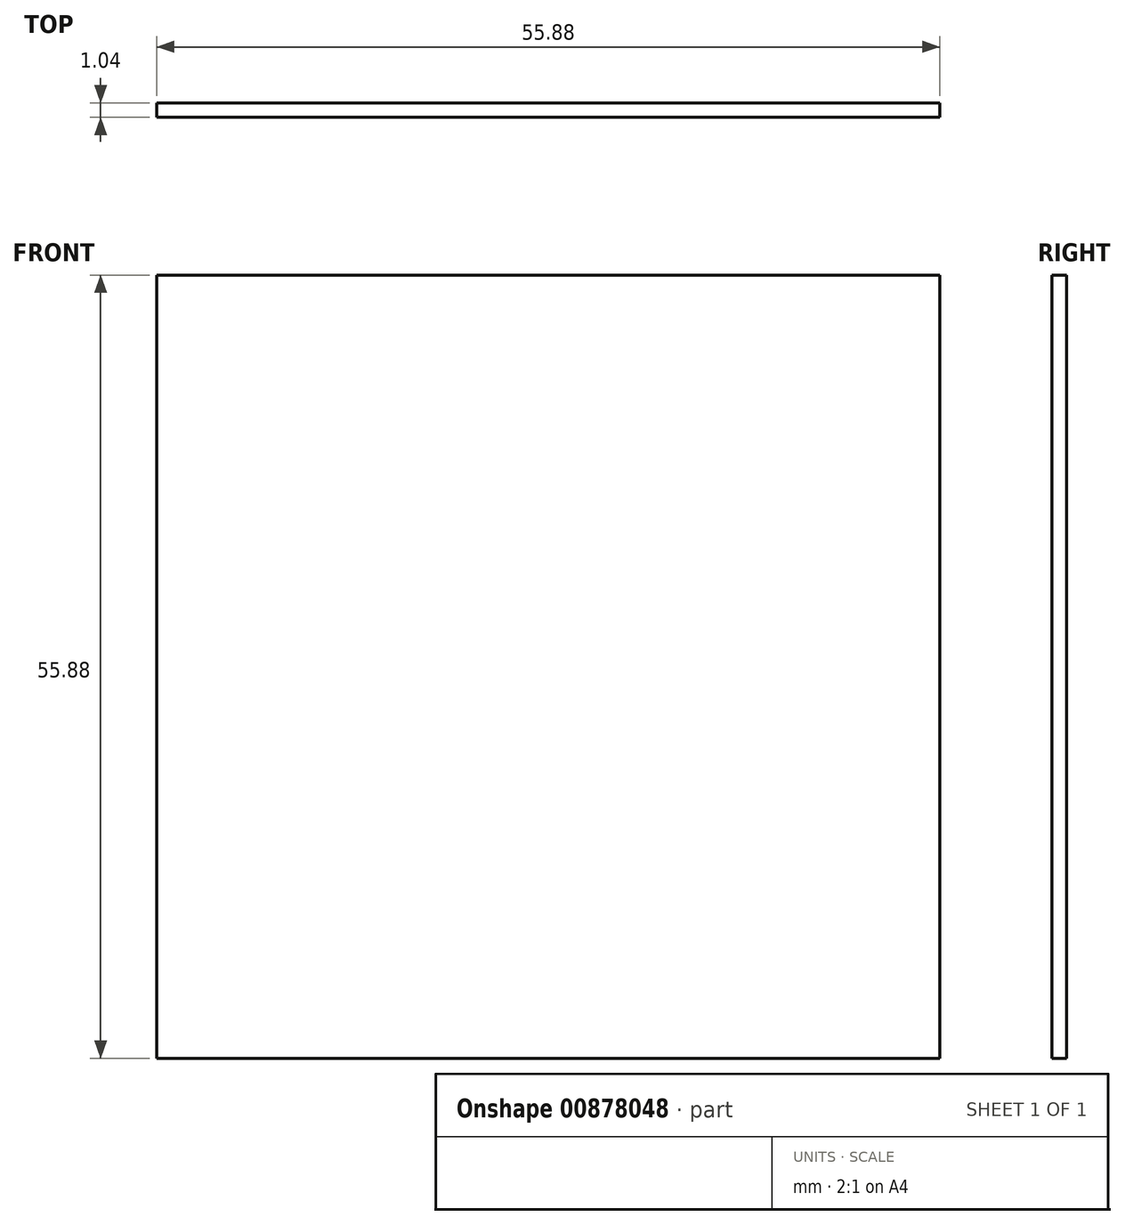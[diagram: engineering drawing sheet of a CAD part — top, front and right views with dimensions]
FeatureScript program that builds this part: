
annotation { "Feature Type Name" : "Feature", "Feature Type Description" : "" }
export const myFeature = defineFeature(function(context is Context, id is Id, definition is map)
    precondition{}
    {
        {
            var Q0;
            Q0=qCreatedBy(makeId("Front.planeOp"),FACE);
            var sketch = newSketch(context, id + "F0", { "sketchPlane" : qUnion([Q0])});
            skLineSegment(sketch, "E0.bottom", {"start": v(0, 0) * mm, "end": v(55.88, 0) * mm});
            skLineSegment(sketch, "E0.top", {"start": v(0, 55.88) * mm, "end": v(55.88, 55.88) * mm});
            skLineSegment(sketch, "E0.left", {"start": v(0, 0) * mm, "end": v(0, 55.88) * mm});
            skLineSegment(sketch, "E0.right", {"start": v(55.88, 0) * mm, "end": v(55.88, 55.88) * mm});
            skSolve(sketch);
        }
        {
            var Q0;
            Q0=makeQuery(id+"F0.imprint","IMPRINT",FACE,{"disambiguationData":[TD([[makeQuery(id+"F0.imprint","IMPRINT",EDGE,{"derivedFrom":sQuery(id+"F0.wireOp",EDGE,"E0.bottom")}),1.0]])]});
            extrude(context, id + "F1", {"entities" : qUnion([Q0]), "depth" : 1.04 * mm, "offsetDistance" : 25.4 * mm});
        }
    });
